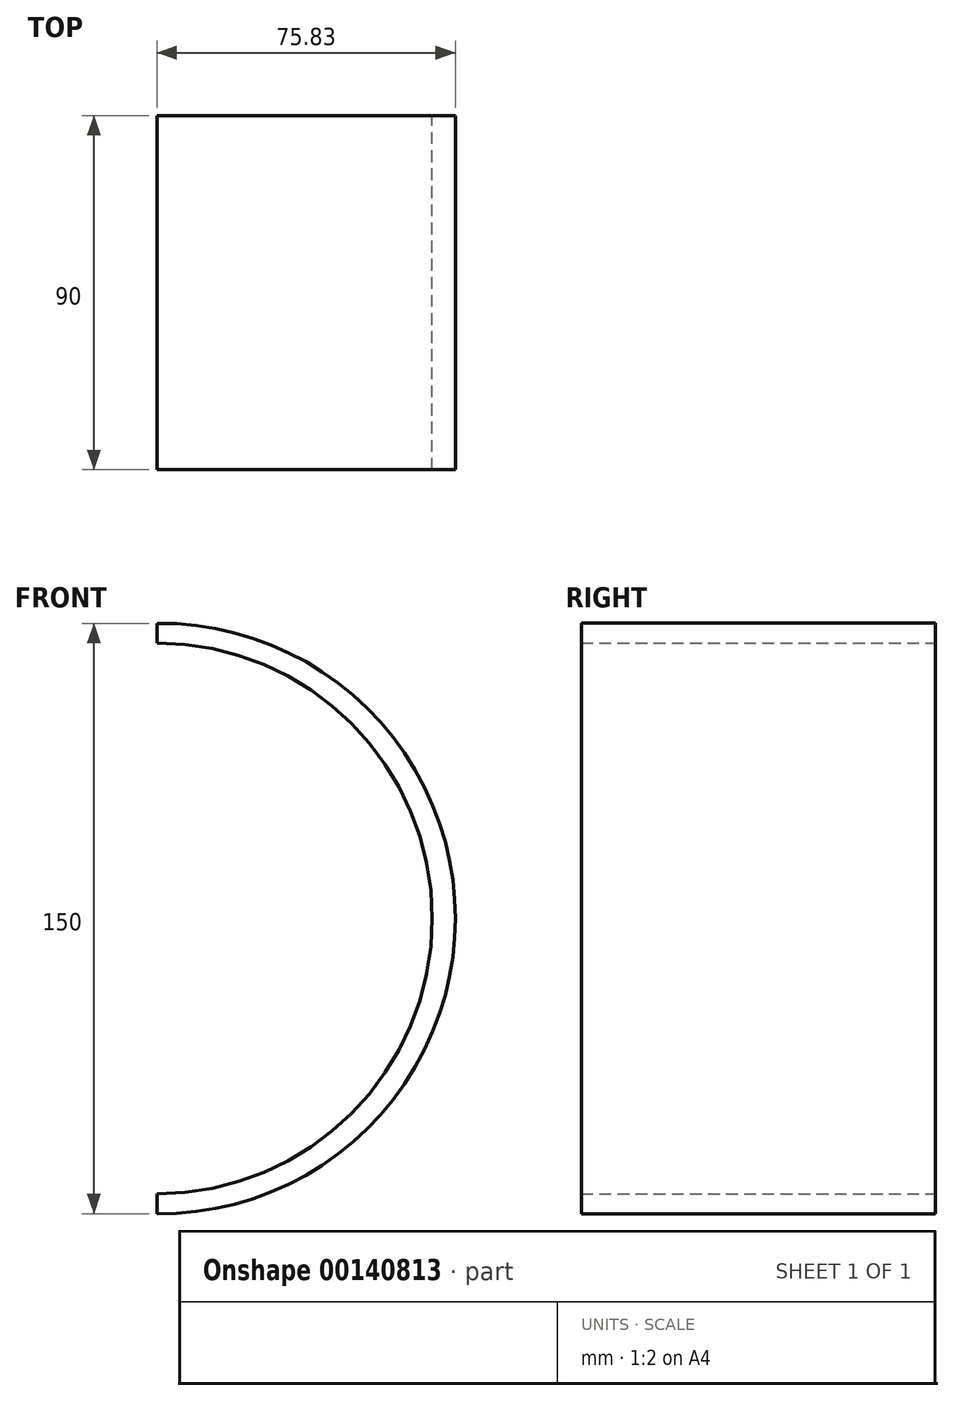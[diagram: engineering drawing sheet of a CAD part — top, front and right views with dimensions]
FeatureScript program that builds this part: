
annotation { "Feature Type Name" : "Feature", "Feature Type Description" : "" }
export const myFeature = defineFeature(function(context is Context, id is Id, definition is map)
    precondition{}
    {
        {
            var Q0;
            Q0=qCreatedBy(makeId("Front.planeOp"),FACE);
            var sketch = newSketch(context, id + "F0", { "sketchPlane" : qUnion([Q0])});
            skLineSegment(sketch, "E0", {"start": v(0, 70) * mm, "end": v(0, 0) * mm, "construction": true});
            skLineSegment(sketch, "E1.MirrorCS", {"start": v(0, -70) * mm, "end": v(0, 0) * mm, "construction": true});
            skLineSegment(sketch, "E2", {"start": v(0, 0) * mm, "end": v(0, 75) * mm});
            skLineSegment(sketch, "E3", {"start": v(0, -70) * mm, "end": v(0, -75) * mm, "construction": true});
            skArc(sketch, "E4", {"start": v(0, -70) * mm, "mid": v(69.97, 0) * mm, "end": v(0, 70) * mm});
            skArc(sketch, "E5", {"start": v(0, -75) * mm, "mid": v(75.83, 0) * mm, "end": v(0, 75) * mm});
            skLineSegment(sketch, "E6", {"start": v(0, 75) * mm, "end": v(0, 70) * mm});
            skLineSegment(sketch, "E7", {"start": v(0, -70) * mm, "end": v(0, -75) * mm});
            skSolve(sketch);
        }
        {
            var Q0;
            Q0=makeQuery(id+"F0.imprint","IMPRINT",FACE,{"disambiguationData":[TD([[makeQuery(id+"F0.imprint","IMPRINT",EDGE,{"derivedFrom":sQuery(id+"F0.wireOp",EDGE,"E4")}),-1.0]])]});
            extrude(context, id + "F1", {"entities" : qUnion([Q0]), "endBound" : BoundingType.SYMMETRIC, "depth" : 90 * mm});
        }
    });
